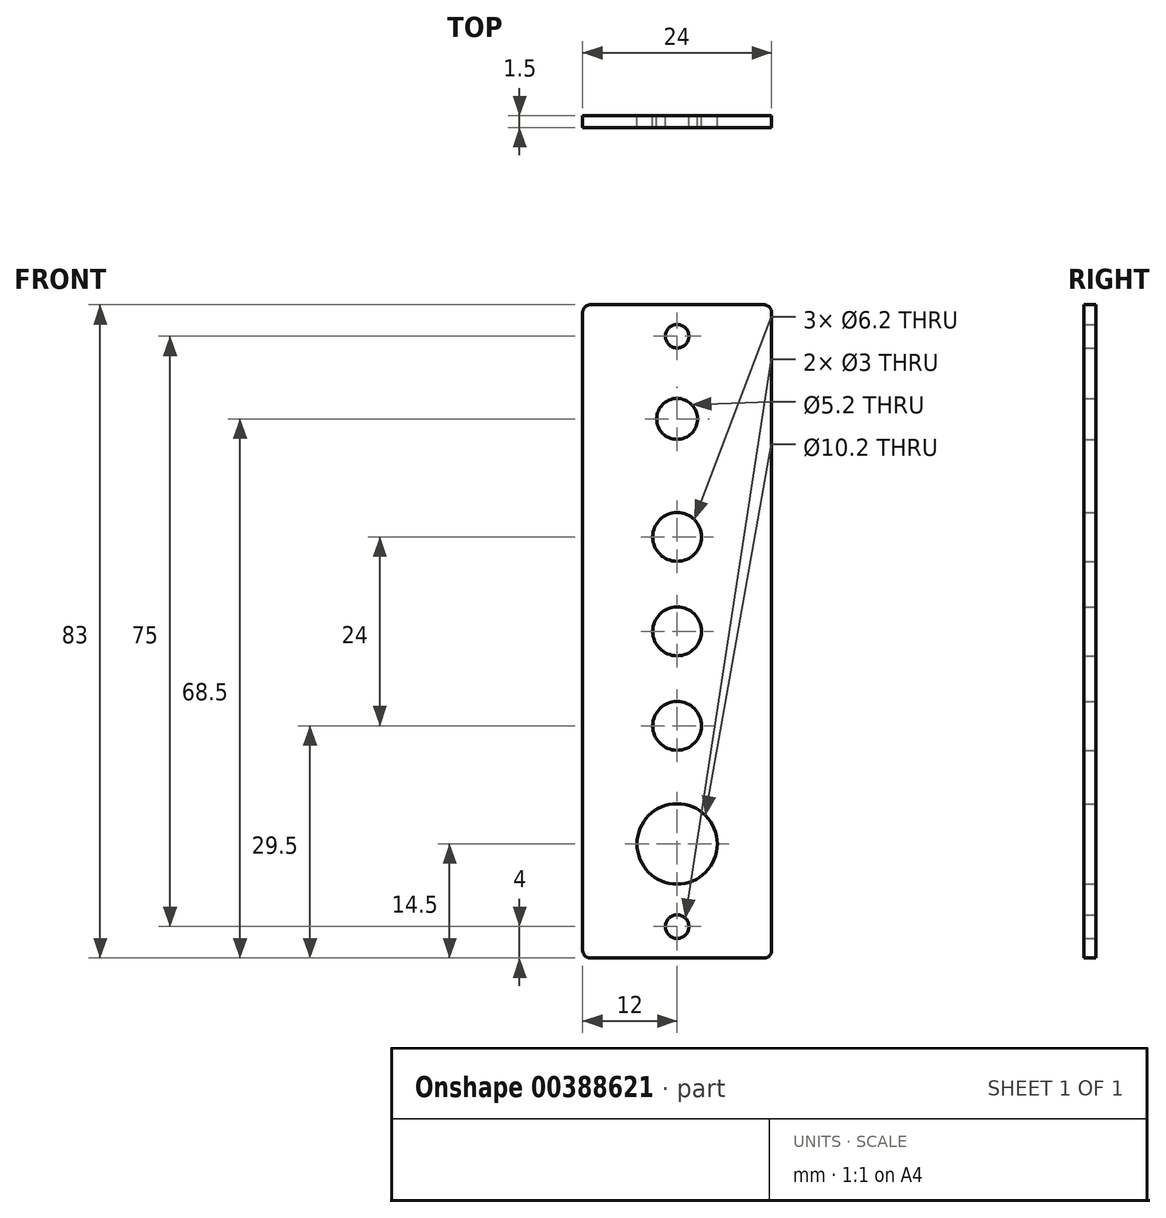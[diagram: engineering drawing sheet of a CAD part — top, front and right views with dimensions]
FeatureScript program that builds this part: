
annotation { "Feature Type Name" : "Feature", "Feature Type Description" : "" }
export const myFeature = defineFeature(function(context is Context, id is Id, definition is map)
    precondition{}
    {
        {
            var Q0;
            Q0=qCreatedBy(makeId("Front.planeOp"),FACE);
            var sketch = newSketch(context, id + "F0", { "sketchPlane" : qUnion([Q0])});
            skLineSegment(sketch, "E0.bottom", {"start": v(12, -41.5) * mm, "end": v(-12, -41.5) * mm});
            skLineSegment(sketch, "E0.top", {"start": v(12, 41.5) * mm, "end": v(-12, 41.5) * mm});
            skLineSegment(sketch, "E0.left", {"start": v(12, -41.5) * mm, "end": v(12, 41.5) * mm});
            skLineSegment(sketch, "E0.right", {"start": v(-12, -41.5) * mm, "end": v(-12, 41.5) * mm});
            skPoint(sketch, "E0.middle", {"position": v(0, 0) * mm});
            skCircle(sketch, "E1", {"center": v(0, 37.5) * mm, "radius": 1.5 * mm});
            skCircle(sketch, "E2", {"center": v(0, -37.5) * mm, "radius": 1.5 * mm});
            skCircle(sketch, "E3", {"center": v(0, 27) * mm, "radius": 2.6 * mm});
            skCircle(sketch, "E4", {"center": v(0, 12) * mm, "radius": 3.1 * mm});
            skCircle(sketch, "E5", {"center": v(0, 0) * mm, "radius": 3.1 * mm});
            skCircle(sketch, "E6", {"center": v(0, -12) * mm, "radius": 3.1 * mm});
            skCircle(sketch, "E7", {"center": v(0, -27) * mm, "radius": 5.1 * mm});
            skSolve(sketch);
        }
        {
            var Q0;
            Q0 = qSketchRegion(id + "F0", true);
            extrude(context, id + "F1", {"entities" : qUnion([Q0]), "depth" : 1.5 * mm});
        }
        {
            var Q0;
            Q0=makeQuery(id+"F1.opExtrude","SWEPT_EDGE",EDGE,{"disambiguationData":[OSD([sQuery(id+"F0.wireOp",EDGE,"E0.top"),sQuery(id+"F0.wireOp",EDGE,"E0.right")])]});
            var Q1;
            Q1=makeQuery(id+"F1.opExtrude","SWEPT_EDGE",EDGE,{"disambiguationData":[OSD([sQuery(id+"F0.wireOp",EDGE,"E0.top"),sQuery(id+"F0.wireOp",EDGE,"E0.left")])]});
            var Q2;
            Q2=makeQuery(id+"F1.opExtrude","SWEPT_EDGE",EDGE,{"disambiguationData":[OSD([sQuery(id+"F0.wireOp",EDGE,"E0.bottom"),sQuery(id+"F0.wireOp",EDGE,"E0.left")])]});
            var Q3;
            Q3=makeQuery(id+"F1.opExtrude","SWEPT_EDGE",EDGE,{"disambiguationData":[OSD([sQuery(id+"F0.wireOp",EDGE,"E0.bottom"),sQuery(id+"F0.wireOp",EDGE,"E0.right")])]});
            fillet(context, id + "F2", {"entities" : qUnion([Q0, Q1, Q2, Q3]), "radius" : 1 * mm, "tangentPropagation" : true, "allowEdgeOverflow" : false});
        }
    });
